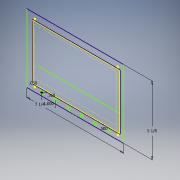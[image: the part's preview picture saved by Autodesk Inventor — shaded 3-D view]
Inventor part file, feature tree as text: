
AUTODESK INVENTOR PART (.ipt)
format: ipt  version: 2019 (Build 230136000, 136)  size: 110,592 bytes
history: native  units: in
note: dims shown in document units (in); Inventor stores cm internally (conversion verified against a paired STEP export)
features: reference x18, other x2, plane x1, sketch x1
ambient origin geometry x8: Origin, YZ Plane, XZ Plane, XY Plane, X Axis, Y Axis, Z Axis, Center Point
feature tree (22):
  plane  "Work Plane1"
  sketch  "Sketch1"  dims[d1=5.125in d2=7.25in d3=0.5in d4=0.2677in d5=2.3622in d7=1.0in d8=0.3937in d10=1.0in d18=0.05in]
  reference  "Reference1"
  reference  "Reference2"
  reference  "Reference3"
  reference  "Reference4"
  reference  "Reference5"
  reference  "Reference6"
  reference  "Reference7"
  reference  "Reference8"
  reference  "Reference9"
  reference  "Reference10"
  reference  "Reference11"
  reference  "Reference12"
  reference  "Reference13"
  reference  "Reference14"
  reference  "Reference15"
  reference  "Reference16"
  reference  "Reference17"
  reference  "Reference18"
  other  "Assembly1"
  other  "NHD-7:1"
